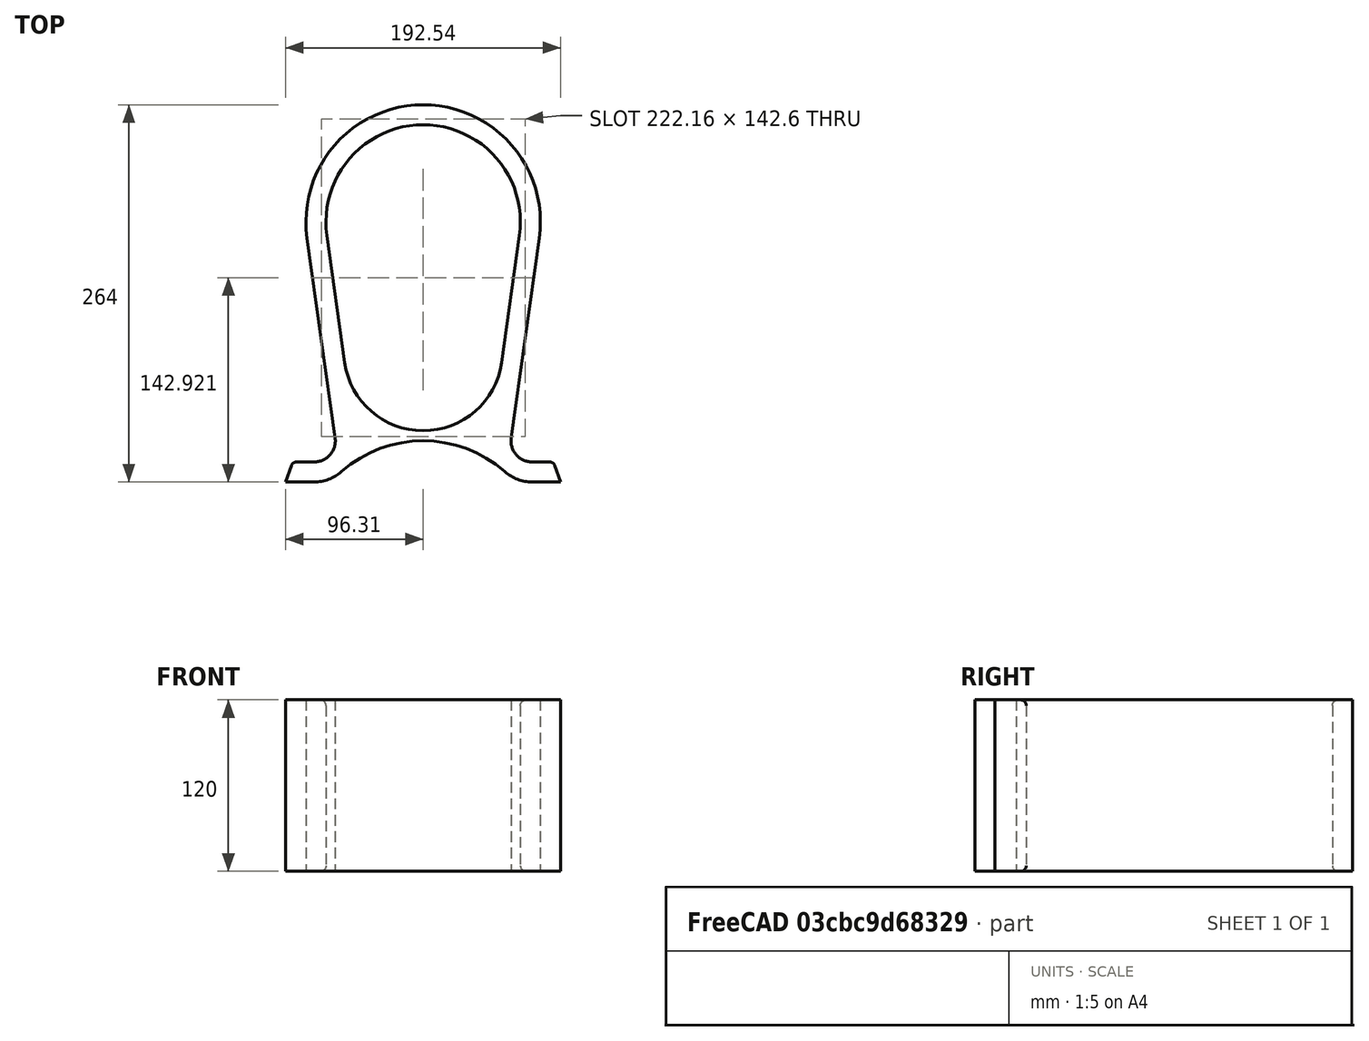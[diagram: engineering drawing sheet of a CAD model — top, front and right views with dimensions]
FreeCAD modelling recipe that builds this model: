
FCSTD DOCUMENT  (FreeCAD 0.22R37898 (Git))
Label: headset stand new version
License: All rights reserved
objects: Sketcher::SketchObject×1, PartDesign::Pad×1, PartDesign::Fillet×1, PartDesign::Body×1
note: 6 computed .brp shape members not serialized (recipe doc carries the construction recipe); baked Part::Feature solids carry a one-line shape summary decoded from their .brp

FEATURE [Sketcher::SketchObject] Sketch
  AttachmentSupport = -> [XY_Plane]
  FullyConstrained = false
  MapMode = 5
  sketch-geometry (34):
    g0: LineSegment StartX=-0.00406372 StartY=175.011 StartZ=0 EndX=63.6948 EndY=0 EndZ=0
    g1: LineSegment StartX=-7.52391e-09 StartY=0 StartZ=0 EndX=0 EndY=250 EndZ=0
    g2: LineSegment StartX=-74.2734 StartY=164.586 StartZ=0 EndX=74.2734 EndY=164.586 EndZ=0
    g3: LineSegment StartX=-27.2941 StartY=100.01 StartZ=0 EndX=27.2941 EndY=100.01 EndZ=0
    g4: LineSegment StartX=-27.2978 StartY=100.01 StartZ=0 EndX=27.2941 EndY=100.01 EndZ=0
    g5: LineSegment StartX=-63.6948 StartY=0 StartZ=0 EndX=0.0120649 EndY=175.033 EndZ=0
    g6: LineSegment StartX=-74.2734 StartY=164.586 StartZ=0 EndX=-54.6716 EndY=24.7909 EndZ=0
    g7: LineSegment StartX=74.2734 StartY=164.586 StartZ=0 EndX=54.6716 EndY=24.7909 EndZ=0
    g8: ArcOfCircle CenterX=1.3e-15 CenterY=175 CenterZ=0 NormalX=0 NormalY=0 NormalZ=1 AngleXU=0 Radius=75 StartAngle=6.14388 EndAngle=9.56409
    g9: ArcOfCircle CenterX=-76.3127 CenterY=21.841 CenterZ=0 NormalX=0 NormalY=0 NormalZ=1 AngleXU=0 Radius=21.841 StartAngle=4.71239 EndAngle=6.4225
    g10: ArcOfCircle CenterX=76.229 CenterY=21.7683 CenterZ=0 NormalX=0 NormalY=0 NormalZ=1 AngleXU=0 Radius=21.7683 StartAngle=3.00228 EndAngle=4.71239
    g11: LineSegment StartX=-98.1537 StartY=21.841 StartZ=0 EndX=97.9972 EndY=21.841 EndZ=0
    g12: LineSegment StartX=76.229 StartY=21.7683 StartZ=0 EndX=76.229 EndY=-2.49e-14 EndZ=0
    g13: LineSegment StartX=-76.3127 StartY=21.841 StartZ=0 EndX=-76.3127 EndY=0 EndZ=0
    g14: ArcOfCircle CenterX=8.5e-15 CenterY=175 CenterZ=0 NormalX=0 NormalY=0 NormalZ=1 AngleXU=0 Radius=82 StartAngle=6.14388 EndAngle=9.56409
    g15: ArcOfCircle CenterX=6.46e-14 CenterY=175 CenterZ=0 NormalX=0 NormalY=0 NormalZ=1 AngleXU=0 Radius=68 StartAngle=6.14388 EndAngle=9.56409
    g16: LineSegment StartX=-76.3114 StartY=-6.98913 StartZ=0 EndX=-96.3114 EndY=-6.98913 EndZ=0
    g17: LineSegment StartX=-76.3127 StartY=7 StartZ=0 EndX=-91.3127 EndY=7 EndZ=0
    g18: LineSegment StartX=76.229 StartY=7 StartZ=0 EndX=91.229 EndY=7 EndZ=0
    g19: LineSegment StartX=76.229 StartY=-7 StartZ=0 EndX=96.229 EndY=-7 EndZ=0
    g20: ArcOfCircle CenterX=-76.3127 CenterY=21.841 CenterZ=0 NormalX=0 NormalY=0 NormalZ=1 AngleXU=0 Radius=14.841 StartAngle=4.71239 EndAngle=6.41685
    g21: ArcOfCircle CenterX=-76.3127 CenterY=21.841 CenterZ=0 NormalX=0 NormalY=0 NormalZ=1 AngleXU=0 Radius=28.8301 StartAngle=4.71243 EndAngle=5.43513
    g22: ArcOfCircle CenterX=76.229 CenterY=21.7683 CenterZ=0 NormalX=0 NormalY=0 NormalZ=1 AngleXU=0 Radius=14.7683 StartAngle=3.00229 EndAngle=4.71239
    g23: LineSegment StartX=-91.3127 StartY=7 StartZ=0 EndX=-96.3114 EndY=-6.98913 EndZ=0
    g24: LineSegment StartX=91.229 StartY=7 StartZ=0 EndX=96.229 EndY=-7 EndZ=0
    g25: LineSegment StartX=-61.604 StartY=23.8189 StartZ=0 EndX=-81.2056 EndY=163.613 EndZ=0
    g26: LineSegment StartX=-67.3412 StartY=165.558 StartZ=0 EndX=-54.8682 EndY=76.5531 EndZ=0
    g27: LineSegment StartX=81.2056 StartY=163.613 StartZ=0 EndX=61.6038 EndY=23.8189 EndZ=0
    g28: LineSegment StartX=67.3412 StartY=165.558 StartZ=0 EndX=54.8606 EndY=76.5489 EndZ=0
    g29: LineSegment StartX=-76.3127 StartY=7 StartZ=0 EndX=76.229 EndY=7 EndZ=0
    g30: LineSegment StartX=-6.86659e-09 StartY=21.841 StartZ=0 EndX=0 EndY=250 EndZ=0
    g31: ArcOfCircle CenterX=-0.0362789 CenterY=-64.6467 CenterZ=0 NormalX=0 NormalY=0 NormalZ=1 AngleXU=0 Radius=86.4877 StartAngle=0.847708 EndAngle=2.29354
    g32: ArcOfCircle CenterX=-0.00353134 CenterY=84.2418 CenterZ=0 NormalX=0 NormalY=0 NormalZ=1 AngleXU=0 Radius=55.4008 StartAngle=3.28082 EndAngle=6.14388
    g33: ArcOfCircle CenterX=76.229 CenterY=21.7683 CenterZ=0 NormalX=0 NormalY=0 NormalZ=1 AngleXU=0 Radius=28.7683 StartAngle=3.9893 EndAngle=4.71239
  constraints (66):
    c: PointOnObject(g30,g-2)
    c: PointOnObject(g0,g-1)
    c: Horizontal(g3)
    c: Horizontal(g4)
    c: PointOnObject(g3,g0)
    c: PointOnObject(g5,g-1)
    c: PointOnObject(g3,g5)
    c: PointOnObject(g4,g3)
    c: PointOnObject(g4,g0)
    c: Coincident(g6,g2)
    c: Coincident(g7,g2)
    c: Coincident(g8,g6) = -1.5708
    c: Block(g6)
    c: Block(g7)
    c: Tangent(g9,g-1)
    c: PointOnObject(g9,g11)
    c: Coincident(g12,g10)
    c: Vertical(g12)
    c: Coincident(g13,g9)
    c: Vertical(g13)
    c: Tangent(g9,g6) = 1.5708
    c: Coincident(g9,g13)
    c: Tangent(g10,g7) = -1.5708
    c: Coincident(g10,g12)
    c: Distance(g16) = 20
    c: Horizontal(g16)
    c: Distance(g17) = 15
    c: Horizontal(g17)
    c: Distance(g18) = 15
    c: Horizontal(g18)
    c: Distance(g19) = 20
    c: Horizontal(g19)
    c: Coincident(g20,g17)
    c: Coincident(g21,g16)
    c: Coincident(g22,g10)
    c: Coincident(g22,g18)
    c: Coincident(g33,g19)
    c: Block(g20)
    c: Block(g21)
    c: Block(g22)
    c: Coincident(g23,g17)
    c: Coincident(g23,g16)
    c: Coincident(g24,g18)
    c: Coincident(g24,g19)
    c: Coincident(g25,g20)
    c: Coincident(g25,g14)
    c: Coincident(g26,g15)
    c: Coincident(g27,g14)
    c: Coincident(g27,g22)
    c: Block(g15)
    c: Block(g14)
    c: Coincident(g28,g15)
    c: Coincident(g29,g17)
    c: Coincident(g29,g18)
    c: PointOnObject(g30,g11)
    c: Block(g11)
    c: Block(g1)
    c: PointOnObject(g30,g1)
    c: Distance(g30,g32) = 7
    c: Tangent(g26,g32) = -1.5708
    c: Tangent(g21,g31) = 1.5708
    c: Tangent(g28,g32) = 1.5708
    c: PointOnObject(g33,g31)
    c: Block(g32)
    c: Block(g31)
    c: Block(g33)
FEATURE [PartDesign::Pad] Pad
  Direction = (0,0,1)
  Length = 120
  Length2 = 10
  Profile = -> Sketch
  ReferenceAxis = -> Sketch [N_Axis]
  Refine = true
  Suppressed = false
  Type = 0
FEATURE [PartDesign::Fillet] Fillet
  Base = -> Pad [Face17,Face16,Face15,Face18,Edge11,Edge32]
  BaseFeature = -> Pad
  Radius = 4
  Refine = true
  SupportTransform = false
  Suppressed = false
  UseAllEdges = false
FEATURE [PartDesign::Body] Body  label="headset stand"
  AllowCompound = false
  Group = -> [Sketch,Pad,Fillet]
  Origin = -> Origin
  Tip = -> Fillet
